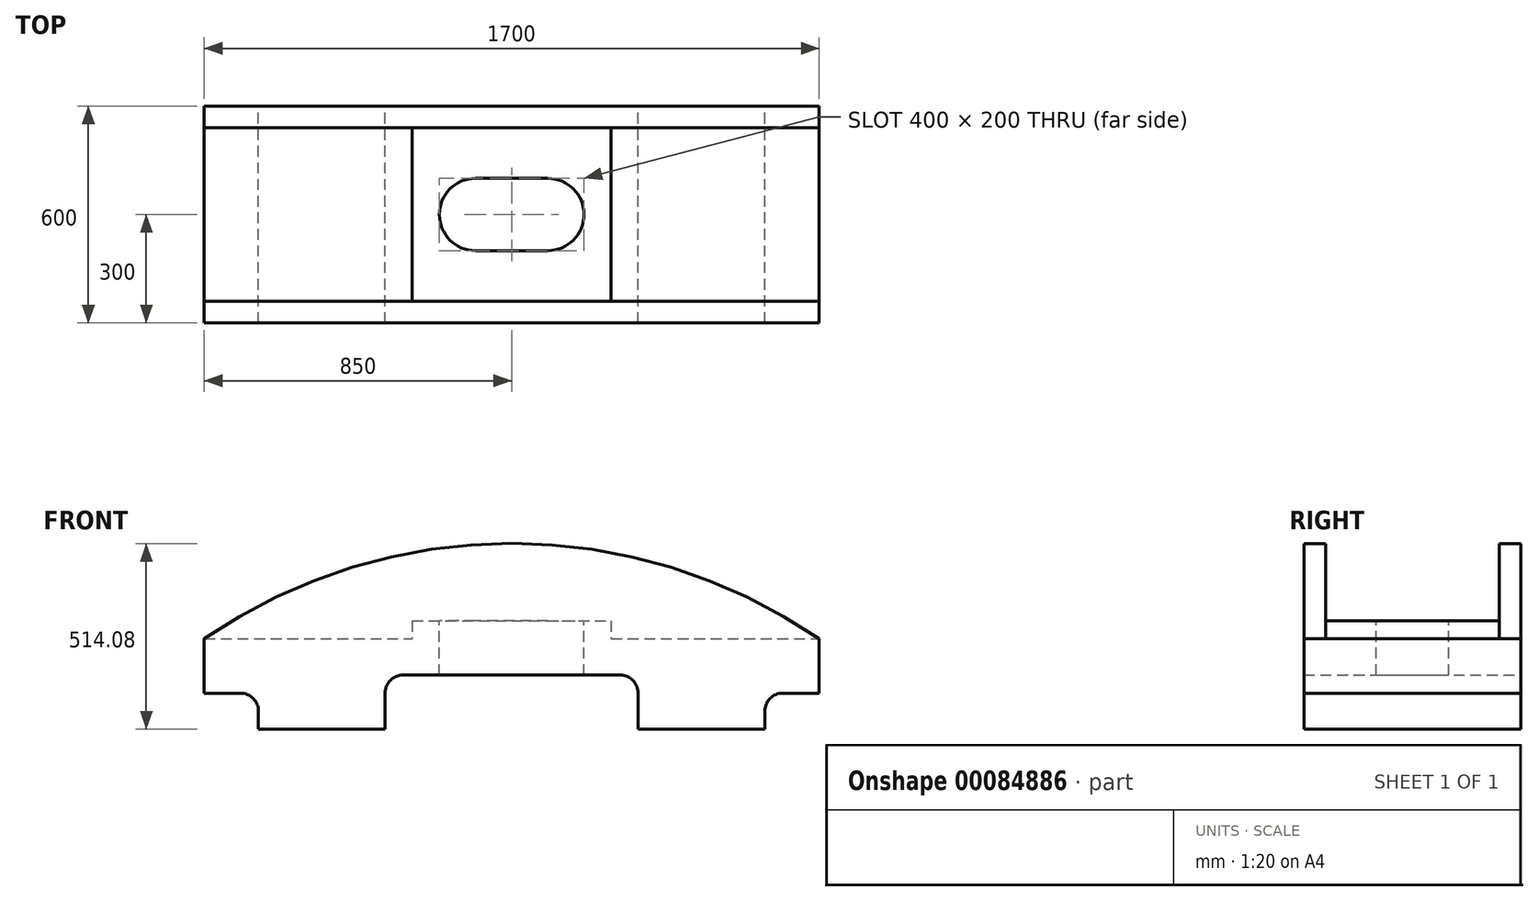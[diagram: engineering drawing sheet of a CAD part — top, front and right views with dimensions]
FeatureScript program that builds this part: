
annotation { "Feature Type Name" : "Feature", "Feature Type Description" : "" }
export const myFeature = defineFeature(function(context is Context, id is Id, definition is map)
    precondition{}
    {
        {
            var Q0;
            Q0=qCreatedBy(makeId("Front.planeOp"),FACE);
            var sketch = newSketch(context, id + "F0", { "sketchPlane" : qUnion([Q0])});
            skLineSegment(sketch, "E0", {"start": v(0, 0) * mm, "end": v(350, 0) * mm});
            skLineSegment(sketch, "E1", {"start": v(350, 0) * mm, "end": v(350, -150) * mm});
            skLineSegment(sketch, "E2", {"start": v(350, -150) * mm, "end": v(700, -150) * mm});
            skLineSegment(sketch, "E3", {"start": v(700, -150) * mm, "end": v(700, -50) * mm});
            skLineSegment(sketch, "E4", {"start": v(700, -50) * mm, "end": v(850, -50) * mm});
            skLineSegment(sketch, "E5", {"start": v(850, -50) * mm, "end": v(850, 100) * mm});
            skPoint(sketch, "E6.endSnap0", {"position": v(175, 0) * mm});
            skLineSegment(sketch, "E7", {"start": v(0, 0) * mm, "end": v(-350, 0) * mm});
            skLineSegment(sketch, "E8", {"start": v(-350, 0) * mm, "end": v(-350, -150) * mm});
            skLineSegment(sketch, "E9", {"start": v(-350, -150) * mm, "end": v(-700, -150) * mm});
            skLineSegment(sketch, "E10", {"start": v(-700, -50) * mm, "end": v(-850, -50) * mm});
            skLineSegment(sketch, "E11", {"start": v(-850, -50) * mm, "end": v(-850, 100) * mm});
            skLineSegment(sketch, "E12", {"start": v(-700, -50) * mm, "end": v(-700, -150) * mm});
            skPoint(sketch, "E13.end.orphan", {"position": v(-675.78, 100) * mm});
            skArc(sketch, "E14", {"start": v(850, 100) * mm, "mid": v(0, 364.08) * mm, "end": v(-850, 100) * mm});
            skSolve(sketch);
        }
        {
            var Q0;
            Q0 = qSketchRegion(id + "F0", true);
            extrude(context, id + "F1", {"entities" : qUnion([Q0]), "endBound" : BoundingType.SYMMETRIC, "depth" : 600 * mm});
        }
        {
            var Q0;
            Q0=qCreatedBy(makeId("Top.planeOp"),FACE);
            var sketch = newSketch(context, id + "F2", { "sketchPlane" : qUnion([Q0])});
            skPoint(sketch, "E15", {"position": v(850, 0) * mm});
            skLineSegment(sketch, "E16", {"start": v(850, 0) * mm, "end": v(850, -240) * mm, "construction": true});
            skLineSegment(sketch, "E17.bottom", {"start": v(850, -240) * mm, "end": v(-850, -240) * mm});
            skLineSegment(sketch, "E17.top", {"start": v(850, 240) * mm, "end": v(-850, 240) * mm});
            skLineSegment(sketch, "E17.left", {"start": v(850, -240) * mm, "end": v(850, 240) * mm});
            skLineSegment(sketch, "E17.right", {"start": v(-850, -240) * mm, "end": v(-850, 240) * mm});
            skPoint(sketch, "E17.middle", {"position": v(0, 0) * mm});
            skSolve(sketch);
        }
        {
            var Q0;
            Q0 = qSketchRegion(id + "F2", true);
            extrude(context, id + "F3", {"entities" : qUnion([Q0]), "operationType" : NewBodyOperationType.REMOVE, "endBound" : BoundingType.THROUGH_ALL, "depth" : 25 * mm});
        }
        {
            var Q0;
            Q0=makeQuery(id+"F3.boolean.opBoolean","COPY",FACE,{"disambiguationData":[OD(1.0)],"derivedFrom":makeQuery(id+"F3.opExtrude","CAP_FACE",FACE,{"disambiguationData":[OSD([sQuery(id+"F2.wireOp",EDGE,"E17.bottom"),sQuery(id+"F2.wireOp",EDGE,"E17.top"),sQuery(id+"F2.wireOp",EDGE,"E17.left"),sQuery(id+"F2.wireOp",EDGE,"E17.right")])],"isStart":true})});
            var sketch = newSketch(context, id + "F4", { "sketchPlane" : qUnion([Q0])});
            skLineSegment(sketch, "E18.bottom", {"start": v(-850, -240) * mm, "end": v(850, -240) * mm});
            skLineSegment(sketch, "E18.top", {"start": v(-850, 240) * mm, "end": v(850, 240) * mm});
            skLineSegment(sketch, "E18.left", {"start": v(-850, -240) * mm, "end": v(-850, 240) * mm});
            skLineSegment(sketch, "E18.right", {"start": v(850, -240) * mm, "end": v(850, 240) * mm});
            skSolve(sketch);
        }
        {
            var Q0;
            Q0 = qSketchRegion(id + "F4", true);
            extrude(context, id + "F5", {"entities" : qUnion([Q0]), "operationType" : NewBodyOperationType.ADD, "depth" : 100 * mm});
        }
        {
            var Q0;
            Q0=makeQuery(id+"F5.opExtrude","CAP_FACE",FACE,{"disambiguationData":[OSD([sQuery(id+"F4.wireOp",EDGE,"E18.bottom"),sQuery(id+"F4.wireOp",EDGE,"E18.top"),sQuery(id+"F4.wireOp",EDGE,"E18.left"),sQuery(id+"F4.wireOp",EDGE,"E18.right")])],"isStart":false});
            var sketch = newSketch(context, id + "F6", { "sketchPlane" : qUnion([Q0])});
            skLineSegment(sketch, "E19.bottom", {"start": v(-275, -240) * mm, "end": v(275, -240) * mm});
            skLineSegment(sketch, "E19.top", {"start": v(-275, 240) * mm, "end": v(275, 240) * mm});
            skLineSegment(sketch, "E19.left", {"start": v(-275, -240) * mm, "end": v(-275, 240) * mm});
            skLineSegment(sketch, "E19.right", {"start": v(275, -240) * mm, "end": v(275, 240) * mm});
            skPoint(sketch, "E19.middle", {"position": v(0, 0) * mm});
            skSolve(sketch);
        }
        {
            var Q0;
            Q0 = qSketchRegion(id + "F6", true);
            extrude(context, id + "F7", {"entities" : qUnion([Q0]), "operationType" : NewBodyOperationType.ADD, "depth" : 50 * mm});
        }
        {
            var Q0;
            Q0=makeQuery(id+"F7.opExtrude","CAP_FACE",FACE,{"disambiguationData":[OSD([sQuery(id+"F6.wireOp",EDGE,"E19.bottom"),sQuery(id+"F6.wireOp",EDGE,"E19.top"),sQuery(id+"F6.wireOp",EDGE,"E19.left"),sQuery(id+"F6.wireOp",EDGE,"E19.right")])],"isStart":false});
            var sketch = newSketch(context, id + "F8", { "sketchPlane" : qUnion([Q0])});
            skLineSegment(sketch, "E20.bottom", {"start": v(100, -100) * mm, "end": v(-100, -100) * mm});
            skLineSegment(sketch, "E20.top", {"start": v(100, 100) * mm, "end": v(-100, 100) * mm});
            skPoint(sketch, "E20.middle", {"position": v(0, 0) * mm});
            skArc(sketch, "E21", {"start": v(-100, 100) * mm, "mid": v(-200, 0) * mm, "end": v(-100, -100) * mm});
            skArc(sketch, "E22", {"start": v(100, -100) * mm, "mid": v(200, 0) * mm, "end": v(100, 100) * mm});
            skSolve(sketch);
        }
        {
            var Q0;
            Q0 = qSketchRegion(id + "F8", true);
            extrude(context, id + "F9", {"entities" : qUnion([Q0]), "operationType" : NewBodyOperationType.REMOVE, "endBound" : BoundingType.THROUGH_ALL, "oppositeDirection" : true, "depth" : 25 * mm});
        }
        {
            var Q0;
            {var subQ0=sQuery(id+"F2.wireOp",EDGE,"E17.top");var subQ1=sQuery(id+"F2.wireOp",EDGE,"E17.bottom");var subQ2=makeQuery(id+"F3.opExtrude","CAP_FACE",FACE,{"disambiguationData":[OSD([subQ1,subQ0,sQuery(id+"F2.wireOp",EDGE,"E17.left"),sQuery(id+"F2.wireOp",EDGE,"E17.right")])],"isStart":true});var subQ3=makeQuery(id+"F3.opExtrude","SWEPT_FACE",FACE,{"disambiguationData":[OSD([subQ1])]});var subQ4=sQuery(id+"F0.wireOp",EDGE,"E8");var subQ5=makeQuery(id+"F1.opExtrude","SWEPT_FACE",FACE,{"disambiguationData":[OSD([subQ4])]});var subQ6=sQuery(id+"F0.wireOp",EDGE,"E7");var subQ7=sQuery(id+"F0.wireOp",EDGE,"E0");var subQ8=makeQuery(id+"F1.opExtrude","SWEPT_FACE",FACE,{"disambiguationData":[OSD([subQ7,subQ6])]});var subQ9=makeQuery(id+"F3.opExtrude","SWEPT_FACE",FACE,{"disambiguationData":[OSD([subQ0])]});var subQ10=makeQuery(id+"F1.opExtrude","SWEPT_EDGE",EDGE,{"disambiguationData":[OSD([subQ6,subQ4])]});var subQ11=sQuery(id+"F0.wireOp",EDGE,"E14");var subQ12=sQuery(id+"F0.wireOp",EDGE,"E12");var subQ13=sQuery(id+"F0.wireOp",EDGE,"E11");var subQ14=sQuery(id+"F0.wireOp",EDGE,"E10");var subQ15=sQuery(id+"F0.wireOp",EDGE,"E9");var subQ16=sQuery(id+"F0.wireOp",EDGE,"E5");var subQ17=sQuery(id+"F0.wireOp",EDGE,"E4");var subQ18=sQuery(id+"F0.wireOp",EDGE,"E3");var subQ19=sQuery(id+"F0.wireOp",EDGE,"E2");var subQ20=sQuery(id+"F0.wireOp",EDGE,"E1");Q0=makeQuery(id+"F5.boolean.opBoolean","MERGE",EDGE,{"derivedFrom":[makeQuery(id+"F3.boolean.opBoolean","SPLIT",EDGE,{"disambiguationData":[TD([makeQuery(id+"F1.opExtrude","CAP_FACE",FACE,{"disambiguationData":[OSD([subQ7,subQ20,subQ19,subQ18,subQ17,subQ16,subQ6,subQ4,subQ15,subQ14,subQ13,subQ12,subQ11])],"isStart":true}),subQ8,subQ5,subQ2,subQ9])],"derivedFrom":subQ10}),makeQuery(id+"F3.boolean.opBoolean","SPLIT",EDGE,{"disambiguationData":[TD([makeQuery(id+"F1.opExtrude","CAP_FACE",FACE,{"disambiguationData":[OSD([subQ7,subQ20,subQ19,subQ18,subQ17,subQ16,subQ6,subQ4,subQ15,subQ14,subQ13,subQ12,subQ11])],"isStart":false}),subQ8,subQ5,subQ3,subQ2])],"derivedFrom":subQ10}),makeQuery(id+"F3.boolean.opBoolean","SPLIT",EDGE,{"disambiguationData":[TD([subQ8,subQ5,subQ3,subQ2,subQ9])],"derivedFrom":subQ10})]});}
            var Q1;
            {var subQ0=sQuery(id+"F2.wireOp",EDGE,"E17.top");var subQ1=sQuery(id+"F2.wireOp",EDGE,"E17.bottom");var subQ2=makeQuery(id+"F3.opExtrude","CAP_FACE",FACE,{"disambiguationData":[OSD([subQ1,subQ0,sQuery(id+"F2.wireOp",EDGE,"E17.left"),sQuery(id+"F2.wireOp",EDGE,"E17.right")])],"isStart":true});var subQ3=makeQuery(id+"F3.opExtrude","SWEPT_FACE",FACE,{"disambiguationData":[OSD([subQ1])]});var subQ4=sQuery(id+"F0.wireOp",EDGE,"E1");var subQ5=makeQuery(id+"F1.opExtrude","SWEPT_FACE",FACE,{"disambiguationData":[OSD([subQ4])]});var subQ6=sQuery(id+"F0.wireOp",EDGE,"E7");var subQ7=sQuery(id+"F0.wireOp",EDGE,"E0");var subQ8=makeQuery(id+"F1.opExtrude","SWEPT_FACE",FACE,{"disambiguationData":[OSD([subQ7,subQ6])]});var subQ9=makeQuery(id+"F3.opExtrude","SWEPT_FACE",FACE,{"disambiguationData":[OSD([subQ0])]});var subQ10=makeQuery(id+"F1.opExtrude","SWEPT_EDGE",EDGE,{"disambiguationData":[OSD([subQ7,subQ4])]});var subQ11=sQuery(id+"F0.wireOp",EDGE,"E14");var subQ12=sQuery(id+"F0.wireOp",EDGE,"E12");var subQ13=sQuery(id+"F0.wireOp",EDGE,"E11");var subQ14=sQuery(id+"F0.wireOp",EDGE,"E10");var subQ15=sQuery(id+"F0.wireOp",EDGE,"E9");var subQ16=sQuery(id+"F0.wireOp",EDGE,"E8");var subQ17=sQuery(id+"F0.wireOp",EDGE,"E5");var subQ18=sQuery(id+"F0.wireOp",EDGE,"E4");var subQ19=sQuery(id+"F0.wireOp",EDGE,"E3");var subQ20=sQuery(id+"F0.wireOp",EDGE,"E2");Q1=makeQuery(id+"F5.boolean.opBoolean","MERGE",EDGE,{"derivedFrom":[makeQuery(id+"F3.boolean.opBoolean","SPLIT",EDGE,{"disambiguationData":[TD([makeQuery(id+"F1.opExtrude","CAP_FACE",FACE,{"disambiguationData":[OSD([subQ7,subQ4,subQ20,subQ19,subQ18,subQ17,subQ6,subQ16,subQ15,subQ14,subQ13,subQ12,subQ11])],"isStart":true}),subQ8,subQ5,subQ2,subQ9])],"derivedFrom":subQ10}),makeQuery(id+"F3.boolean.opBoolean","SPLIT",EDGE,{"disambiguationData":[TD([makeQuery(id+"F1.opExtrude","CAP_FACE",FACE,{"disambiguationData":[OSD([subQ7,subQ4,subQ20,subQ19,subQ18,subQ17,subQ6,subQ16,subQ15,subQ14,subQ13,subQ12,subQ11])],"isStart":false}),subQ8,subQ5,subQ3,subQ2])],"derivedFrom":subQ10}),makeQuery(id+"F3.boolean.opBoolean","SPLIT",EDGE,{"disambiguationData":[TD([subQ8,subQ5,subQ3,subQ2,subQ9])],"derivedFrom":subQ10})]});}
            var Q2;
            Q2=makeQuery(id+"F1.opExtrude","SWEPT_EDGE",EDGE,{"disambiguationData":[OSD([sQuery(id+"F0.wireOp",EDGE,"E10"),sQuery(id+"F0.wireOp",EDGE,"E12")])]});
            var Q3;
            Q3=makeQuery(id+"F1.opExtrude","SWEPT_EDGE",EDGE,{"disambiguationData":[OSD([sQuery(id+"F0.wireOp",EDGE,"E3"),sQuery(id+"F0.wireOp",EDGE,"E4")])]});
            fillet(context, id + "F10", {"entities" : qUnion([Q0, Q1, Q2, Q3]), "radius" : 50 * mm, "tangentPropagation" : true, "allowEdgeOverflow" : false});
        }
    });
